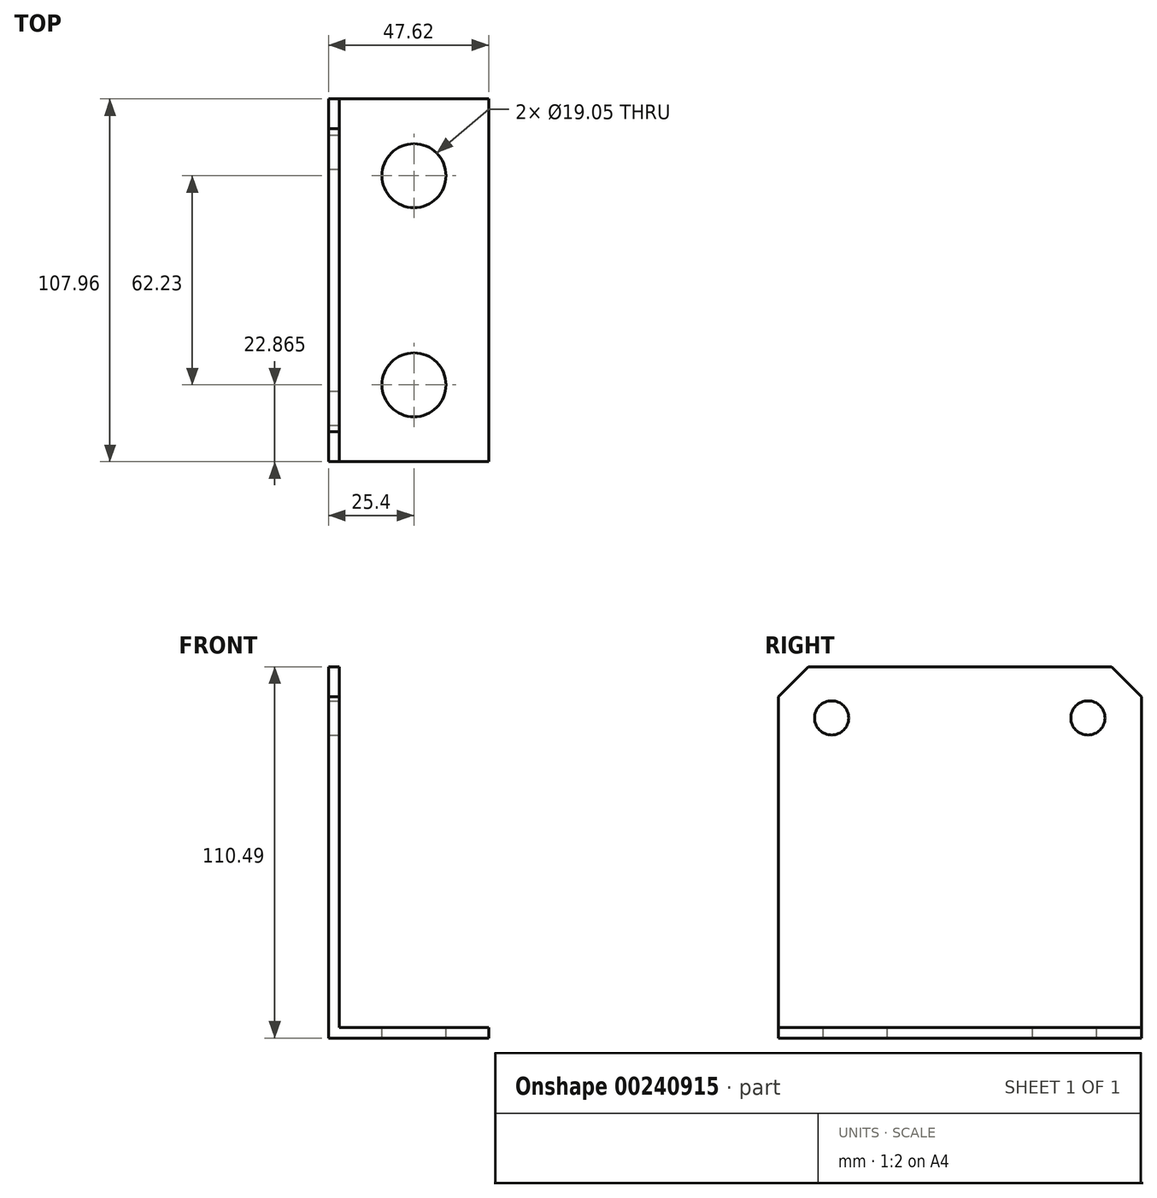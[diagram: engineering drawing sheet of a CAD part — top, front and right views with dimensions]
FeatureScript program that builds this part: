
annotation { "Feature Type Name" : "Feature", "Feature Type Description" : "" }
export const myFeature = defineFeature(function(context is Context, id is Id, definition is map)
    precondition{}
    {
        {
            var Q0;
            Q0=qCreatedBy(makeId("Right.planeOp"),FACE);
            var sketch = newSketch(context, id + "F0", { "sketchPlane" : qUnion([Q0])});
            skLineSegment(sketch, "E0.bottom", {"start": v(28.57, 63.5) * mm, "end": v(-28.57, 63.5) * mm});
            skLineSegment(sketch, "E0.top", {"start": v(53.97, -63.5) * mm, "end": v(-53.97, -63.5) * mm});
            skLineSegment(sketch, "E0.left", {"start": v(53.98, 38.1) * mm, "end": v(53.98, -63.5) * mm});
            skLineSegment(sketch, "E0.right", {"start": v(-53.98, 38.1) * mm, "end": v(-53.97, -63.5) * mm});
            skPoint(sketch, "E0.middle", {"position": v(0, 0) * mm});
            skLineSegment(sketch, "E1", {"start": v(0, 0) * mm, "end": v(0, 94.6) * mm, "construction": true});
            skPoint(sketch, "E1.endSnap0", {"position": v(0, 63.5) * mm});
            skLineSegment(sketch, "E2", {"start": v(-53.98, 38.1) * mm, "end": v(-28.57, 63.5) * mm});
            skLineSegment(sketch, "E3.MirrorCS", {"start": v(53.97, 38.1) * mm, "end": v(28.57, 63.5) * mm});
            skPoint(sketch, "E4.orphan", {"position": v(-53.98, 63.5) * mm});
            skPoint(sketch, "E5.orphan", {"position": v(53.98, 63.5) * mm});
            skSolve(sketch);
        }
        {
            var Q0;
            Q0=qSketchRegion(id+"F0",true);
            extrude(context, id + "F1", {"entities" : qUnion([Q0]), "depth" : 3.17 * mm});
        }
        {
            var Q0;
            Q0=makeQuery(id+"F1.opExtrude","SWEPT_FACE",FACE,{"disambiguationData":[OSD([sQuery(id+"F0.wireOp",EDGE,"E0.right")])]});
            var sketch = newSketch(context, id + "F2", { "sketchPlane" : qUnion([Q0])});
            skLineSegment(sketch, "E6", {"start": v(3.18, -63.5) * mm, "end": v(47.62, -63.5) * mm});
            skLineSegment(sketch, "E7", {"start": v(47.62, -63.5) * mm, "end": v(47.62, -60.33) * mm});
            skLineSegment(sketch, "E8", {"start": v(47.62, -60.33) * mm, "end": v(3.17, -60.33) * mm});
            skLineSegment(sketch, "E9", {"start": v(3.17, -60.33) * mm, "end": v(3.18, -63.5) * mm});
            skSolve(sketch);
        }
        {
            var Q0;
            Q0=qSketchRegion(id+"F2",true);
            var Q1;
            Q1=makeQuery(id+"F1.opExtrude","SWEPT_FACE",FACE,{"disambiguationData":[OSD([sQuery(id+"F0.wireOp",EDGE,"E0.left")])]});
            extrude(context, id + "F3", {"entities" : qUnion([Q0]), "operationType" : NewBodyOperationType.ADD, "endBound" : BoundingType.UP_TO_SURFACE, "oppositeDirection" : true, "endBoundEntityFace" : qUnion([Q1]), "depth" : 25.4 * mm});
        }
        {
            var Q0;
            Q0=makeQuery(id+"F1.opExtrude","CAP_FACE",FACE,{"disambiguationData":[OSD([sQuery(id+"F0.wireOp",EDGE,"E0.bottom"),sQuery(id+"F0.wireOp",EDGE,"E0.top"),sQuery(id+"F0.wireOp",EDGE,"E0.left"),sQuery(id+"F0.wireOp",EDGE,"E0.right")])],"isStart":false});
            var sketch = newSketch(context, id + "F4", { "sketchPlane" : qUnion([Q0])});
            skCircle(sketch, "E10", {"center": v(-38.1, 31.75) * mm, "radius": 5.08 * mm});
            skCircle(sketch, "E11", {"center": v(38.1, 31.75) * mm, "radius": 5.08 * mm});
            skSolve(sketch);
        }
        {
            var Q0;
            Q0=qSketchRegion(id+"F4",true);
            var Q1;
            Q1=makeQuery(id+"F1.opExtrude","CAP_FACE",FACE,{"disambiguationData":[OSD([sQuery(id+"F0.wireOp",EDGE,"E0.bottom"),sQuery(id+"F0.wireOp",EDGE,"E0.top"),sQuery(id+"F0.wireOp",EDGE,"E0.left"),sQuery(id+"F0.wireOp",EDGE,"E0.right"),sQuery(id+"F0.wireOp",EDGE,"E2"),sQuery(id+"F0.wireOp",EDGE,"E3.MirrorCS")])],"isStart":true});
            extrude(context, id + "F5", {"entities" : qUnion([Q0]), "operationType" : NewBodyOperationType.REMOVE, "endBound" : BoundingType.UP_TO_SURFACE, "oppositeDirection" : true, "endBoundEntityFace" : qUnion([Q1]), "depth" : 25.4 * mm});
        }
        {
            var Q0;
            Q0=makeQuery(id+"F3.opExtrude","SWEPT_FACE",FACE,{"disambiguationData":[OSD([sQuery(id+"F2.wireOp",EDGE,"E8")])]});
            var sketch = newSketch(context, id + "F6", { "sketchPlane" : qUnion([Q0])});
            skLineSegment(sketch, "E12", {"start": v(0, 0) * mm, "end": v(0, 50.21) * mm, "construction": true});
            skPoint(sketch, "E13.centerSnap0", {"position": v(25.4, -53.97) * mm});
            skLineSegment(sketch, "E14", {"start": v(0, 0) * mm, "end": v(-46.47, 0) * mm, "construction": true});
            skCircle(sketch, "E15", {"center": v(25.4, 31.11) * mm, "radius": 9.53 * mm});
            skPoint(sketch, "E15.centerSnap0", {"position": v(25.4, 53.97) * mm});
            skCircle(sketch, "E16.MirrorC", {"center": v(25.4, -31.11) * mm, "radius": 9.53 * mm});
            skSolve(sketch);
        }
        {
            var Q0;
            Q0=qSketchRegion(id+"F6",true);
            var Q1;
            Q1=makeQuery(id+"F3.boolean.opBoolean","MERGE",FACE,{"derivedFrom":[makeQuery(id+"F1.opExtrude","SWEPT_FACE",FACE,{"disambiguationData":[OSD([sQuery(id+"F0.wireOp",EDGE,"E0.top")])]}),makeQuery(id+"F3.opExtrude","SWEPT_FACE",FACE,{"disambiguationData":[OSD([sQuery(id+"F2.wireOp",EDGE,"E6")])]})]});
            extrude(context, id + "F7", {"entities" : qUnion([Q0]), "operationType" : NewBodyOperationType.REMOVE, "endBound" : BoundingType.UP_TO_SURFACE, "oppositeDirection" : true, "endBoundEntityFace" : qUnion([Q1]), "depth" : 25.4 * mm});
        }
        {
            var Q0;
            Q0=qSketchRegion(id+"F6",true);
            var Q1;
            Q1=makeQuery(id+"F3.boolean.opBoolean","MERGE",FACE,{"derivedFrom":[makeQuery(id+"F1.opExtrude","SWEPT_FACE",FACE,{"disambiguationData":[OSD([sQuery(id+"F0.wireOp",EDGE,"E0.top")])]}),makeQuery(id+"F3.opExtrude","SWEPT_FACE",FACE,{"disambiguationData":[OSD([sQuery(id+"F2.wireOp",EDGE,"E6")])]})]});
            extrude(context, id + "F8", {"entities" : qUnion([Q0]), "operationType" : NewBodyOperationType.REMOVE, "endBound" : BoundingType.UP_TO_SURFACE, "oppositeDirection" : true, "endBoundEntityFace" : qUnion([Q1]), "depth" : 25.4 * mm});
        }
        {
            var Q0;
            Q0=makeQuery(id+"F1.opExtrude","CAP_FACE",FACE,{"disambiguationData":[OSD([sQuery(id+"F0.wireOp",EDGE,"E0.bottom"),sQuery(id+"F0.wireOp",EDGE,"E0.top"),sQuery(id+"F0.wireOp",EDGE,"E0.left"),sQuery(id+"F0.wireOp",EDGE,"E0.right"),sQuery(id+"F0.wireOp",EDGE,"E2"),sQuery(id+"F0.wireOp",EDGE,"E3.MirrorCS")])],"isStart":false});
            var sketch = newSketch(context, id + "F9", { "sketchPlane" : qUnion([Q0])});
            skLineSegment(sketch, "E17", {"start": v(-28.57, 63.5) * mm, "end": v(28.57, 63.5) * mm});
            skLineSegment(sketch, "E18", {"start": v(28.57, 63.5) * mm, "end": v(45.09, 46.99) * mm});
            skLineSegment(sketch, "E19", {"start": v(45.09, 46.99) * mm, "end": v(-45.09, 46.99) * mm});
            skLineSegment(sketch, "E20", {"start": v(-45.09, 46.99) * mm, "end": v(-28.57, 63.5) * mm});
            skSolve(sketch);
        }
        {
            var Q0;
            Q0=qSketchRegion(id+"F9",true);
            var Q1;
            Q1=makeQuery(id+"F1.opExtrude","CAP_FACE",FACE,{"disambiguationData":[OSD([sQuery(id+"F0.wireOp",EDGE,"E0.bottom"),sQuery(id+"F0.wireOp",EDGE,"E0.top"),sQuery(id+"F0.wireOp",EDGE,"E0.left"),sQuery(id+"F0.wireOp",EDGE,"E0.right"),sQuery(id+"F0.wireOp",EDGE,"E2"),sQuery(id+"F0.wireOp",EDGE,"E3.MirrorCS")])],"isStart":true});
            extrude(context, id + "F10", {"entities" : qUnion([Q0]), "operationType" : NewBodyOperationType.REMOVE, "endBound" : BoundingType.UP_TO_SURFACE, "oppositeDirection" : true, "endBoundEntityFace" : qUnion([Q1]), "depth" : 25.4 * mm});
        }
    });
